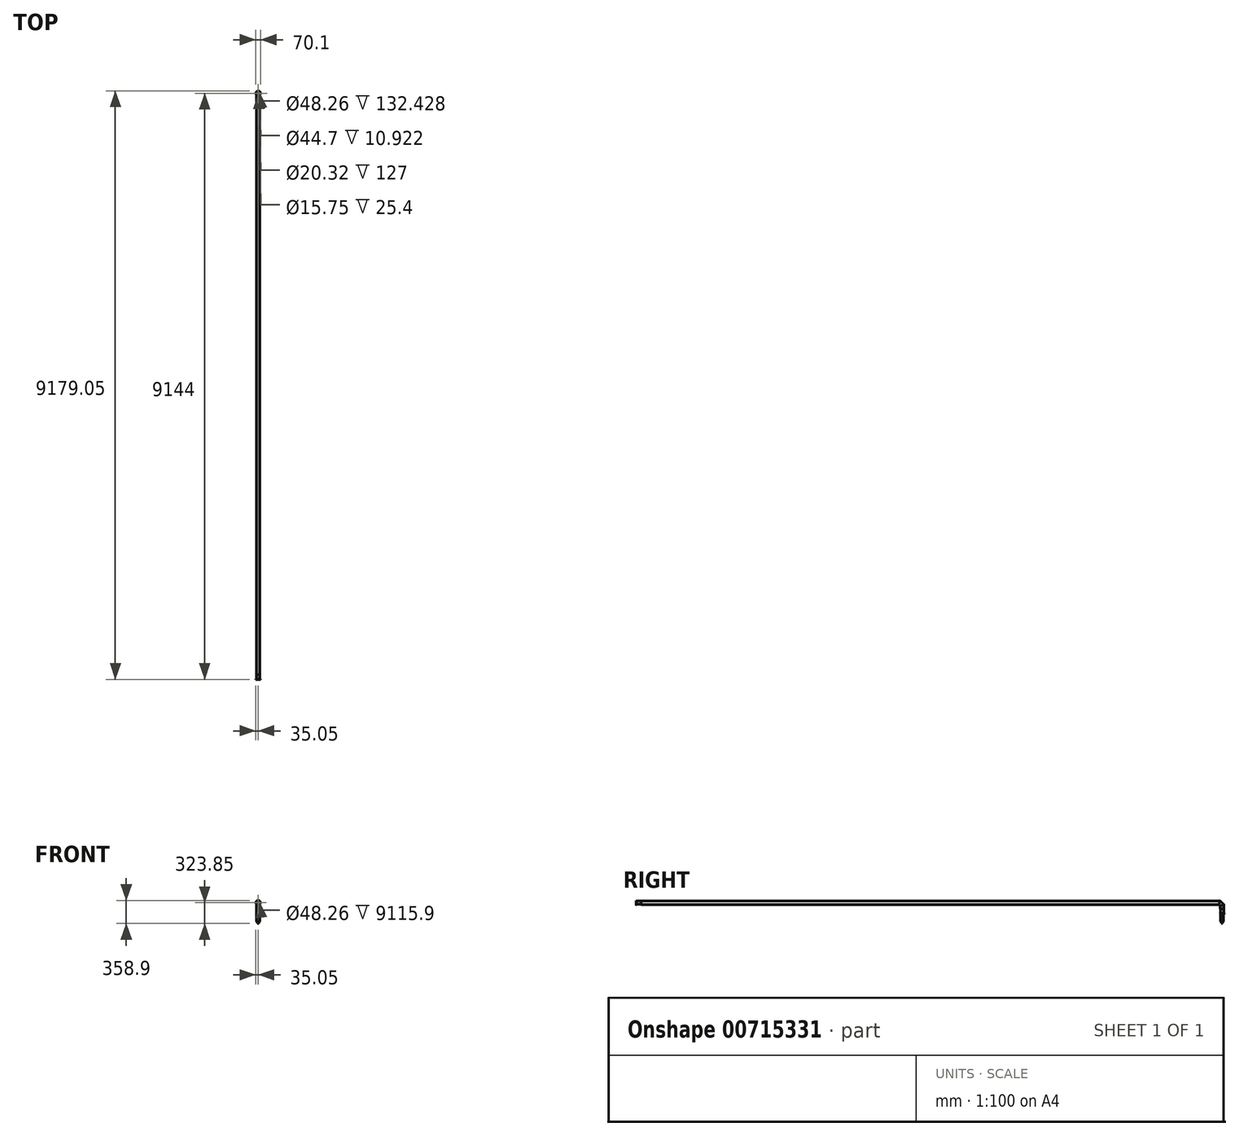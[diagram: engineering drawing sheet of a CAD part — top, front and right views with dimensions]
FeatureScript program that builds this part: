
annotation { "Feature Type Name" : "Feature", "Feature Type Description" : "" }
export const myFeature = defineFeature(function(context is Context, id is Id, definition is map)
    precondition{}
    {
        {
            var Q0;
            Q0=qCreatedBy(makeId("Front.planeOp"),FACE);
            var sketch = newSketch(context, id + "F0", { "sketchPlane" : qUnion([Q0])});
            skCircle(sketch, "E0", {"center": v(0, 0) * mm, "radius": 22.23 * mm, "construction": true});
            skSolve(sketch);
        }
        {
            var Q0;
            Q0=qCreatedBy(makeId("Front.planeOp"),FACE);
            var sketch = newSketch(context, id + "F1", { "sketchPlane" : qUnion([Q0])});
            skCircle(sketch, "E1", {"center": v(0, 0) * mm, "radius": 24.13 * mm});
            skCircle(sketch, "E2", {"center": v(0, 0) * mm, "radius": 35.05 * mm});
            skSolve(sketch);
        }
        {
            var Q0;
            Q0=qSketchRegion(id+"F1",true);
            extrude(context, id + "F2", {"entities" : qUnion([Q0]), "oppositeDirection" : true, "depth" : 5.84 * mm, "offsetDistance" : 25.4 * mm});
        }
        {
            var Q0;
            Q0=makeQuery(id+"F2.opExtrude","CAP_EDGE",EDGE,{"disambiguationData":[OSD([sQuery(id+"F1.wireOp",EDGE,"E2")])],"isStart":false});
            chamfer(context, id + "F3", {"entities" : qUnion([Q0]), "chamferType" : ChamferType.OFFSET_ANGLE, "width" : 2.54 * mm, "oppositeDirection" : false, "angle" : 70 * degree, "tangentPropagation" : true});
        }
        {
            var Q0;
            Q0=makeQuery(id+"F2.opExtrude","CAP_FACE",FACE,{"disambiguationData":[OSD([sQuery(id+"F1.wireOp",EDGE,"E1"),sQuery(id+"F1.wireOp",EDGE,"E2")])],"isStart":false});
            var sketch = newSketch(context, id + "F4", { "sketchPlane" : qUnion([Q0])});
            skCircle(sketch, "E3", {"center": v(0, 0) * mm, "radius": 28.07 * mm});
            skCircle(sketch, "E4", {"center": v(0, 0) * mm, "radius": 24.13 * mm});
            skSolve(sketch);
        }
        {
            var Q0;
            Q0=qSketchRegion(id+"F4",true);
            extrude(context, id + "F5", {"entities" : qUnion([Q0]), "operationType" : NewBodyOperationType.ADD, "depth" : 2.54 * mm, "offsetDistance" : 25.4 * mm});
        }
        {
            var Q0;
            Q0=makeQuery(id+"F5.opExtrude","CAP_FACE",FACE,{"disambiguationData":[OSD([sQuery(id+"F4.wireOp",EDGE,"E3"),sQuery(id+"F4.wireOp",EDGE,"E4")])],"isStart":false});
            var sketch = newSketch(context, id + "F6", { "sketchPlane" : qUnion([Q0])});
            skCircle(sketch, "E5", {"center": v(0, 0) * mm, "radius": 26.55 * mm});
            skCircle(sketch, "E6", {"center": v(0, 0) * mm, "radius": 24.13 * mm});
            skSolve(sketch);
        }
        {
            var Q0;
            Q0=qSketchRegion(id+"F6",true);
            extrude(context, id + "F7", {"entities" : qUnion([Q0]), "operationType" : NewBodyOperationType.ADD, "depth" : 2.54 * mm, "offsetDistance" : 25.4 * mm});
        }
        {
            var Q0;
            Q0=makeQuery(id+"F7.opExtrude","CAP_FACE",FACE,{"disambiguationData":[OSD([sQuery(id+"F6.wireOp",EDGE,"E5"),sQuery(id+"F6.wireOp",EDGE,"E6")])],"isStart":false});
            var sketch = newSketch(context, id + "F8", { "sketchPlane" : qUnion([Q0])});
            skCircle(sketch, "E7", {"center": v(0, 0) * mm, "radius": 24.13 * mm});
            skCircle(sketch, "E8", {"center": v(0, 0) * mm, "radius": 25.4 * mm});
            skSolve(sketch);
        }
        {
            var Q0;
            Q0=qSketchRegion(id+"F8",true);
            extrude(context, id + "F9", {"entities" : qUnion([Q0]), "operationType" : NewBodyOperationType.ADD, "depth" : 65.28 * mm, "offsetDistance" : 25.4 * mm});
        }
        {
            var Q0;
            Q0=makeQuery(id+"F9.opExtrude","CAP_FACE",FACE,{"disambiguationData":[OSD([sQuery(id+"F8.wireOp",EDGE,"E7"),sQuery(id+"F8.wireOp",EDGE,"E8")])],"isStart":false});
            var sketch = newSketch(context, id + "F10", { "sketchPlane" : qUnion([Q0])});
            skCircle(sketch, "E9", {"center": v(0, 0) * mm, "radius": 27.94 * mm});
            skCircle(sketch, "E10", {"center": v(0, 0) * mm, "radius": 24.13 * mm});
            skSolve(sketch);
        }
        {
            var Q0;
            Q0=qCreatedBy(makeId("Right.planeOp"),FACE);
            var sketch = newSketch(context, id + "F11", { "sketchPlane" : qUnion([Q0])});
            skLineSegment(sketch, "E11", {"start": v(0, 0) * mm, "end": v(9144, 0) * mm, "construction": true});
            skLineSegment(sketch, "E12", {"start": v(9144, 0) * mm, "end": v(9144, -95.25) * mm, "construction": true});
            skLineSegment(sketch, "E13", {"start": v(9105.9, 0) * mm, "end": v(9144, -38.1) * mm});
            skLineSegment(sketch, "E14", {"start": v(9144, -38.1) * mm, "end": v(9144, -95.25) * mm});
            skLineSegment(sketch, "E15", {"start": v(76.2, 0) * mm, "end": v(9105.9, 0) * mm});
            skSolve(sketch);
        }
        {
            var Q0;
            Q0=qSketchRegion(id+"F10",true);
            var Q1;
            Q1=qConstructionFilter(qBodyType(qCreatedBy(id+"F11",EDGE),BodyType.WIRE),ConstructionObject.NO);
            sweep(context, id + "F12", {"operationType" : NewBodyOperationType.ADD, "profiles" : qUnion([Q0]), "path" : qUnion([Q1])});
        }
        {
            var Q0;
            Q0=makeQuery(id+"F12.opSweep","CAP_EDGE",EDGE,{"disambiguationData":[OSD([sQuery(id+"F10.wireOp",EDGE,"E9"),sQuery(id+"F11.wireOp",VERTEX,"E15.start")])],"isStart":true});
            fillet(context, id + "F13", {"entities" : qUnion([Q0]), "radius" : 1.27 * mm, "tangentPropagation" : true, "allowEdgeOverflow" : false});
        }
        {
            var Q0;
            Q0=makeQuery(id+"F12.opSweep","CAP_FACE",FACE,{"disambiguationData":[OSD([sQuery(id+"F10.wireOp",EDGE,"E9"),sQuery(id+"F10.wireOp",EDGE,"E10"),sQuery(id+"F11.wireOp",VERTEX,"E14.end")])],"isStart":false});
            var sketch = newSketch(context, id + "F14", { "sketchPlane" : qUnion([Q0])});
            skCircle(sketch, "E16", {"center": v(0, -9144) * mm, "radius": 24.13 * mm});
            skCircle(sketch, "E17", {"center": v(0, -9144) * mm, "radius": 25.4 * mm});
            skSolve(sketch);
        }
        {
            var Q0;
            Q0=makeQuery(id+"F12.opSweep","CAP_EDGE",EDGE,{"disambiguationData":[OSD([sQuery(id+"F10.wireOp",EDGE,"E9"),sQuery(id+"F11.wireOp",VERTEX,"E14.end")])],"isStart":false});
            fillet(context, id + "F15", {"entities" : qUnion([Q0]), "radius" : 1.27 * mm, "tangentPropagation" : true, "allowEdgeOverflow" : false});
        }
        {
            var Q0;
            Q0=qSketchRegion(id+"F14",true);
            extrude(context, id + "F16", {"entities" : qUnion([Q0]), "operationType" : NewBodyOperationType.ADD, "depth" : 76.2 * mm, "offsetDistance" : 25.4 * mm});
        }
        {
            var Q0;
            Q0=makeQuery(id+"F16.opExtrude","CAP_FACE",FACE,{"disambiguationData":[OSD([sQuery(id+"F14.wireOp",EDGE,"E16"),sQuery(id+"F14.wireOp",EDGE,"E17")])],"isStart":false});
            var sketch = newSketch(context, id + "F17", { "sketchPlane" : qUnion([Q0])});
            skCircle(sketch, "E18", {"center": v(0, -9144) * mm, "radius": 35.05 * mm});
            skCircle(sketch, "E19", {"center": v(0, -9144) * mm, "radius": 22.35 * mm});
            skSolve(sketch);
        }
        {
            var Q0;
            Q0=qSketchRegion(id+"F17",true);
            extrude(context, id + "F18", {"entities" : qUnion([Q0]), "operationType" : NewBodyOperationType.ADD, "oppositeDirection" : true, "depth" : 5.84 * mm, "offsetDistance" : 25.4 * mm});
        }
        {
            var Q0;
            Q0=makeQuery(id+"F18.opExtrude","CAP_EDGE",EDGE,{"disambiguationData":[OSD([sQuery(id+"F17.wireOp",EDGE,"E18")])],"isStart":false});
            chamfer(context, id + "F19", {"entities" : qUnion([Q0]), "chamferType" : ChamferType.OFFSET_ANGLE, "width" : 2.54 * mm, "oppositeDirection" : false, "angle" : 70 * degree, "tangentPropagation" : true});
        }
        {
            var Q0;
            Q0=makeQuery(id+"F18.opExtrude","CAP_FACE",FACE,{"disambiguationData":[OSD([sQuery(id+"F17.wireOp",EDGE,"E18"),sQuery(id+"F17.wireOp",EDGE,"E19")])],"isStart":false});
            var sketch = newSketch(context, id + "F20", { "sketchPlane" : qUnion([Q0])});
            skCircle(sketch, "E20", {"center": v(0, 9144) * mm, "radius": 22.35 * mm});
            skCircle(sketch, "E21", {"center": v(0, 9144) * mm, "radius": 28.07 * mm});
            skSolve(sketch);
        }
        {
            var Q0;
            Q0=qSketchRegion(id+"F20",true);
            extrude(context, id + "F21", {"entities" : qUnion([Q0]), "operationType" : NewBodyOperationType.ADD, "depth" : 2.54 * mm, "offsetDistance" : 25.4 * mm});
        }
        {
            var Q0;
            Q0=makeQuery(id+"F21.opExtrude","CAP_FACE",FACE,{"disambiguationData":[OSD([sQuery(id+"F20.wireOp",EDGE,"E20"),sQuery(id+"F20.wireOp",EDGE,"E21")])],"isStart":false});
            var sketch = newSketch(context, id + "F22", { "sketchPlane" : qUnion([Q0])});
            skCircle(sketch, "E22", {"center": v(0, 9144) * mm, "radius": 22.35 * mm});
            skCircle(sketch, "E23", {"center": v(0, 9144) * mm, "radius": 26.8 * mm});
            skSolve(sketch);
        }
        {
            var Q0;
            Q0=qSketchRegion(id+"F22",true);
            extrude(context, id + "F23", {"entities" : qUnion([Q0]), "operationType" : NewBodyOperationType.ADD, "depth" : 2.54 * mm, "offsetDistance" : 25.4 * mm});
        }
        {
            var Q0;
            Q0=makeQuery(id+"F18.boolean.opBoolean","MERGE",FACE,{"derivedFrom":[makeQuery(id+"F16.opExtrude","CAP_FACE",FACE,{"disambiguationData":[OSD([sQuery(id+"F14.wireOp",EDGE,"E16"),sQuery(id+"F14.wireOp",EDGE,"E17")])],"isStart":false}),makeQuery(id+"F18.opExtrude","CAP_FACE",FACE,{"disambiguationData":[OSD([sQuery(id+"F17.wireOp",EDGE,"E18"),sQuery(id+"F17.wireOp",EDGE,"E19")])],"isStart":true})]});
            var sketch = newSketch(context, id + "F24", { "sketchPlane" : qUnion([Q0])});
            skCircle(sketch, "E24", {"center": v(0, -9144) * mm, "radius": 10.16 * mm});
            skCircle(sketch, "E25", {"center": v(0, -9144) * mm, "radius": 24.13 * mm});
            skSolve(sketch);
        }
        {
            var Q0;
            Q0=qSketchRegion(id+"F24",true);
            extrude(context, id + "F25", {"entities" : qUnion([Q0]), "operationType" : NewBodyOperationType.ADD, "depth" : 127 * mm, "offsetDistance" : 25.4 * mm});
        }
        {
            var Q0;
            Q0=makeQuery(id+"F25.opExtrude","CAP_FACE",FACE,{"disambiguationData":[OSD([sQuery(id+"F24.wireOp",EDGE,"E24"),sQuery(id+"F24.wireOp",EDGE,"E25")])],"isStart":false});
            var sketch = newSketch(context, id + "F26", { "sketchPlane" : qUnion([Q0])});
            skCircle(sketch, "E26", {"center": v(0, -9144) * mm, "radius": 10.67 * mm});
            skCircle(sketch, "E27", {"center": v(0, -9144) * mm, "radius": 7.87 * mm});
            skSolve(sketch);
        }
        {
            var Q0;
            Q0=qSketchRegion(id+"F26",true);
            extrude(context, id + "F27", {"entities" : qUnion([Q0]), "operationType" : NewBodyOperationType.ADD, "depth" : 25.4 * mm, "offsetDistance" : 25.4 * mm});
        }
    });
